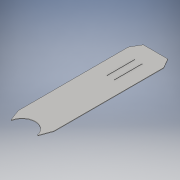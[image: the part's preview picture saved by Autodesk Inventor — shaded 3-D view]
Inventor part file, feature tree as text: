
AUTODESK INVENTOR PART (.ipt)
format: ipt  version: 2016 (Build 200138000, 138)  size: 150,016 bytes
history: native  units: in
note: dims shown in document units (in); Inventor stores cm internally (conversion verified against a paired STEP export)
features: extrude x2, sketch x2, other x1, projected_geometry x1
ambient origin geometry x8: Origin, YZ Plane, XZ Plane, XY Plane, X Axis, Y Axis, Z Axis, Center Point
bodies: Body1 (feature_tree)
feature tree (6):
  other  "Blade.ipt"
  extrude  "Extrusion2"  TaperAngle=150.0deg  [1 undecoded]
  extrude  "Extrusion3"  Depth=5.0in
  sketch  "Sketch2"  dims[d9=1.0994in d10=150.0deg]
  sketch  "Sketch5"  dims[d11=0.125in d13=6.25in d14=6.0in d15=0.1969in d16=0.0in d26=0.3937in d27=9.8193in d28=2.5in d29=0.12in d30=0.12in d31=5.0in d32=4.0in d34=1.0in d35=0.0in]
  projected_geometry  "Projected Loop1"
note: 1 required parameter value undecoded (feature->parameter linkage not recoverable at this tier; creation-order binding heuristic only, values carry confidence <= 0.55)
